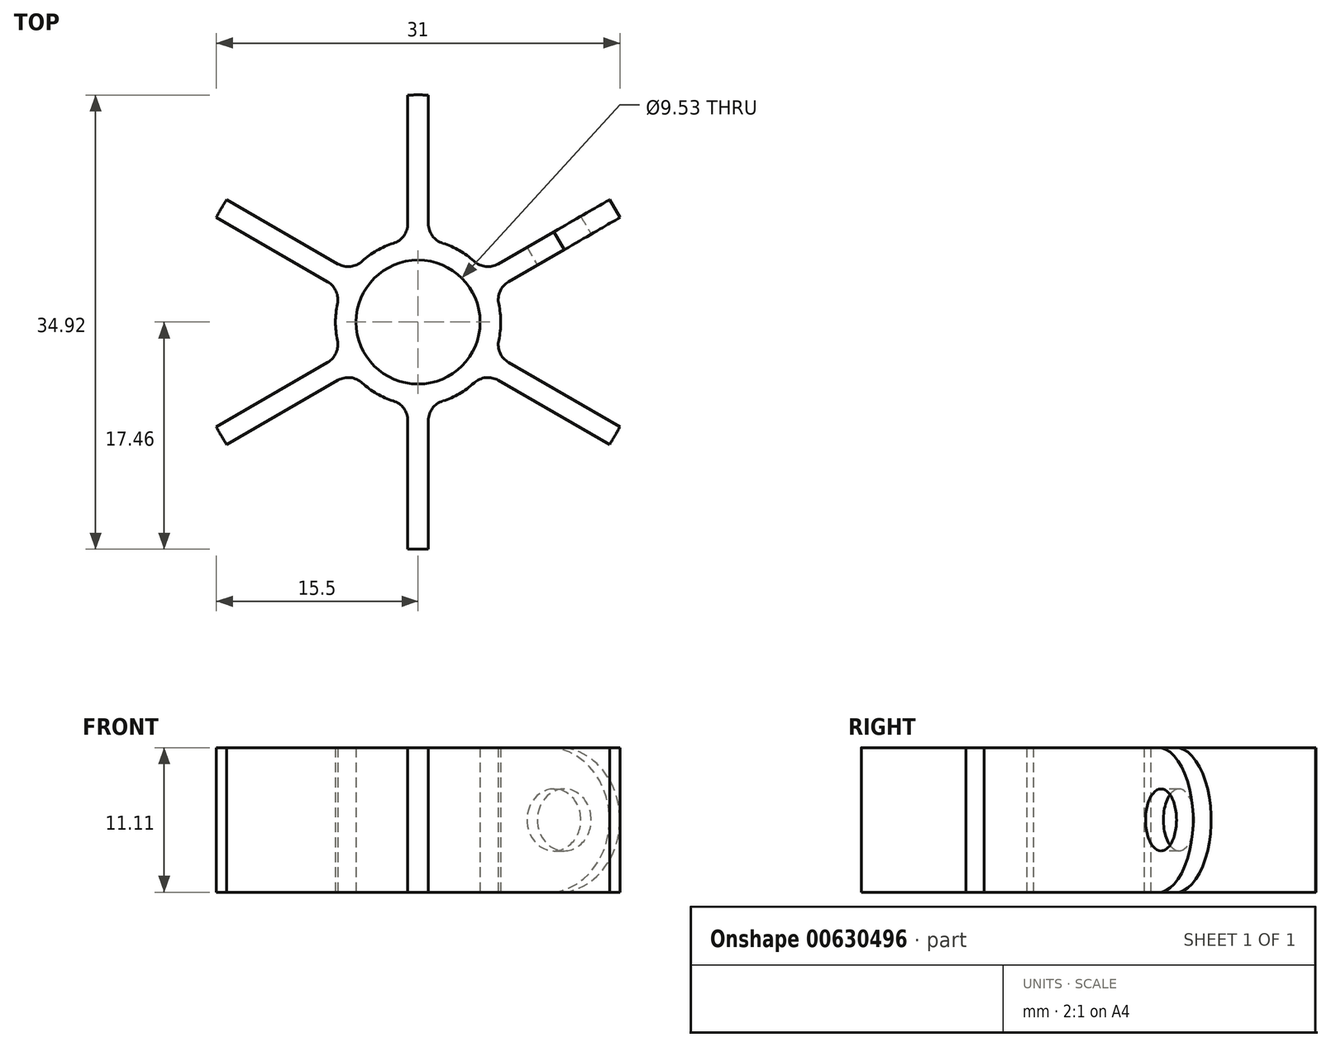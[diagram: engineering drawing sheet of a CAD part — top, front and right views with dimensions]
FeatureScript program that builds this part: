
annotation { "Feature Type Name" : "Feature", "Feature Type Description" : "" }
export const myFeature = defineFeature(function(context is Context, id is Id, definition is map)
    precondition{}
    {
        {
            var Q0;
            Q0=qCreatedBy(makeId("Top.planeOp"),FACE);
            var sketch = newSketch(context, id + "F0", { "sketchPlane" : qUnion([Q0])});
            skArc(sketch, "E0", {"start": v(-0.8, 6.3) * mm, "mid": v(-3.17, 5.5) * mm, "end": v(-5.06, 3.84) * mm});
            skLineSegment(sketch, "E1", {"start": v(0, 0) * mm, "end": v(0, 17.46) * mm, "construction": true});
            skArc(sketch, "E2", {"start": v(0.8, 17.44) * mm, "mid": v(0, 17.46) * mm, "end": v(-0.8, 17.44) * mm});
            skLineSegment(sketch, "E3", {"start": v(-0.8, 17.44) * mm, "end": v(-0.8, 6.3) * mm});
            skLineSegment(sketch, "E4", {"start": v(0.8, 17.44) * mm, "end": v(0.8, 6.3) * mm});
            skLineSegment(sketch, "E5.1.0", {"start": v(-14.71, 9.4) * mm, "end": v(-5.06, 3.84) * mm});
            skLineSegment(sketch, "E5.1.1", {"start": v(-15.5, 8.03) * mm, "end": v(-5.85, 2.46) * mm});
            skArc(sketch, "E5.1.2", {"start": v(-14.71, 9.4) * mm, "mid": v(-15.12, 8.73) * mm, "end": v(-15.5, 8.03) * mm});
            skLineSegment(sketch, "E5.1.3", {"start": v(0, 0) * mm, "end": v(-15.12, 8.73) * mm, "construction": true});
            skLineSegment(sketch, "E5.2.0", {"start": v(-15.5, -8.03) * mm, "end": v(-5.85, -2.46) * mm});
            skLineSegment(sketch, "E5.2.1", {"start": v(-14.71, -9.4) * mm, "end": v(-5.06, -3.84) * mm});
            skArc(sketch, "E5.2.2", {"start": v(-15.5, -8.03) * mm, "mid": v(-15.12, -8.73) * mm, "end": v(-14.71, -9.4) * mm});
            skLineSegment(sketch, "E5.2.3", {"start": v(0, 0) * mm, "end": v(-15.12, -8.73) * mm, "construction": true});
            skLineSegment(sketch, "E5.3.0", {"start": v(-0.8, -17.44) * mm, "end": v(-0.8, -6.3) * mm});
            skLineSegment(sketch, "E5.3.1", {"start": v(0.8, -17.44) * mm, "end": v(0.8, -6.3) * mm});
            skArc(sketch, "E5.3.2", {"start": v(-0.8, -17.44) * mm, "mid": v(0, -17.46) * mm, "end": v(0.8, -17.44) * mm});
            skLineSegment(sketch, "E5.3.3", {"start": v(0, 0) * mm, "end": v(0, -17.46) * mm, "construction": true});
            skLineSegment(sketch, "E5.4.0", {"start": v(14.71, -9.4) * mm, "end": v(5.06, -3.84) * mm});
            skLineSegment(sketch, "E5.4.1", {"start": v(15.5, -8.03) * mm, "end": v(5.85, -2.46) * mm});
            skArc(sketch, "E5.4.2", {"start": v(14.71, -9.4) * mm, "mid": v(15.12, -8.73) * mm, "end": v(15.5, -8.03) * mm});
            skLineSegment(sketch, "E5.4.3", {"start": v(0, 0) * mm, "end": v(15.12, -8.73) * mm, "construction": true});
            skLineSegment(sketch, "E5.5.0", {"start": v(15.5, 8.03) * mm, "end": v(5.85, 2.46) * mm});
            skLineSegment(sketch, "E5.5.1", {"start": v(14.71, 9.4) * mm, "end": v(5.06, 3.84) * mm});
            skArc(sketch, "E5.5.2", {"start": v(15.5, 8.03) * mm, "mid": v(15.12, 8.73) * mm, "end": v(14.71, 9.4) * mm});
            skLineSegment(sketch, "E5.5.3", {"start": v(0, 0) * mm, "end": v(15.12, 8.73) * mm, "construction": true});
            skArc(sketch, "E6.trimOffspring", {"start": v(5.06, 3.84) * mm, "mid": v(3.17, 5.5) * mm, "end": v(0.8, 6.3) * mm});
            skArc(sketch, "E7.trimOffspring", {"start": v(5.85, -2.46) * mm, "mid": v(6.35, 0) * mm, "end": v(5.85, 2.46) * mm});
            skArc(sketch, "E8.trimOffspring", {"start": v(0.8, -6.3) * mm, "mid": v(3.17, -5.5) * mm, "end": v(5.06, -3.84) * mm});
            skArc(sketch, "E9.trimOffspring", {"start": v(-5.06, -3.84) * mm, "mid": v(-3.18, -5.5) * mm, "end": v(-0.8, -6.3) * mm});
            skArc(sketch, "E10.trimOffspring", {"start": v(-5.85, 2.46) * mm, "mid": v(-6.35, 0) * mm, "end": v(-5.85, -2.46) * mm});
            skCircle(sketch, "E11", {"center": v(0, 0) * mm, "radius": 4.76 * mm});
            skSolve(sketch);
        }
        {
            var Q0;
            Q0=makeQuery(id+"F0.imprint","IMPRINT",FACE,{"disambiguationData":[TD([[makeQuery(id+"F0.imprint","IMPRINT",EDGE,{"derivedFrom":sQuery(id+"F0.wireOp",EDGE,"E0")}),1.0]])]});
            extrude(context, id + "F1", {"entities" : qUnion([Q0]), "depth" : 11.1 * mm, "offsetDistance" : 25.4 * mm});
        }
        {
            var Q0;
            Q0=makeQuery(id+"F1.opExtrude","SWEPT_EDGE",EDGE,{"disambiguationData":[OSD([sQuery(id+"F0.wireOp",EDGE,"E0"),sQuery(id+"F0.wireOp",EDGE,"E5.1.0")])]});
            var Q1;
            Q1=makeQuery(id+"F1.opExtrude","SWEPT_EDGE",EDGE,{"disambiguationData":[OSD([sQuery(id+"F0.wireOp",EDGE,"E4"),sQuery(id+"F0.wireOp",EDGE,"E6.trimOffspring")])]});
            var Q2;
            Q2=makeQuery(id+"F1.opExtrude","SWEPT_EDGE",EDGE,{"disambiguationData":[OSD([sQuery(id+"F0.wireOp",EDGE,"E5.5.1"),sQuery(id+"F0.wireOp",EDGE,"E6.trimOffspring")])]});
            var Q3;
            Q3=makeQuery(id+"F1.opExtrude","SWEPT_EDGE",EDGE,{"disambiguationData":[OSD([sQuery(id+"F0.wireOp",EDGE,"E5.4.1"),sQuery(id+"F0.wireOp",EDGE,"E7.trimOffspring")])]});
            var Q4;
            Q4=makeQuery(id+"F1.opExtrude","SWEPT_EDGE",EDGE,{"disambiguationData":[OSD([sQuery(id+"F0.wireOp",EDGE,"E5.5.0"),sQuery(id+"F0.wireOp",EDGE,"E7.trimOffspring")])]});
            var Q5;
            Q5=makeQuery(id+"F1.opExtrude","SWEPT_EDGE",EDGE,{"disambiguationData":[OSD([sQuery(id+"F0.wireOp",EDGE,"E5.3.1"),sQuery(id+"F0.wireOp",EDGE,"E8.trimOffspring")])]});
            var Q6;
            Q6=makeQuery(id+"F1.opExtrude","SWEPT_EDGE",EDGE,{"disambiguationData":[OSD([sQuery(id+"F0.wireOp",EDGE,"E5.4.0"),sQuery(id+"F0.wireOp",EDGE,"E8.trimOffspring")])]});
            var Q7;
            Q7=makeQuery(id+"F1.opExtrude","SWEPT_EDGE",EDGE,{"disambiguationData":[OSD([sQuery(id+"F0.wireOp",EDGE,"E5.3.0"),sQuery(id+"F0.wireOp",EDGE,"E9.trimOffspring")])]});
            var Q8;
            Q8=makeQuery(id+"F1.opExtrude","SWEPT_EDGE",EDGE,{"disambiguationData":[OSD([sQuery(id+"F0.wireOp",EDGE,"E5.2.1"),sQuery(id+"F0.wireOp",EDGE,"E9.trimOffspring")])]});
            var Q9;
            Q9=makeQuery(id+"F1.opExtrude","SWEPT_EDGE",EDGE,{"disambiguationData":[OSD([sQuery(id+"F0.wireOp",EDGE,"E5.2.0"),sQuery(id+"F0.wireOp",EDGE,"E10.trimOffspring")])]});
            var Q10;
            Q10=makeQuery(id+"F1.opExtrude","SWEPT_EDGE",EDGE,{"disambiguationData":[OSD([sQuery(id+"F0.wireOp",EDGE,"E5.1.1"),sQuery(id+"F0.wireOp",EDGE,"E10.trimOffspring")])]});
            var Q11;
            Q11=makeQuery(id+"F1.opExtrude","SWEPT_EDGE",EDGE,{"disambiguationData":[OSD([sQuery(id+"F0.wireOp",EDGE,"E0"),sQuery(id+"F0.wireOp",EDGE,"E3")])]});
            fillet(context, id + "F2", {"entities" : qUnion([Q0, Q1, Q2, Q3, Q4, Q5, Q6, Q7, Q8, Q9, Q10, Q11]), "radius" : 1.59 * mm, "tangentPropagation" : true, "allowEdgeOverflow" : false});
        }
        {
            var Q0;
            Q0=makeQuery(id+"F1.opExtrude","SWEPT_FACE",FACE,{"disambiguationData":[OSD([sQuery(id+"F0.wireOp",EDGE,"E5.5.0")])]});
            var sketch = newSketch(context, id + "F3", { "sketchPlane" : qUnion([Q0])});
            skCircle(sketch, "E12", {"center": v(12.5, 5.56) * mm, "radius": 2.38 * mm});
            skPoint(sketch, "E12.centerSnap0", {"position": v(17.44, 5.56) * mm});
            skPoint(sketch, "E12.centerSnap1", {"position": v(12.5, 11.11) * mm});
            skArc(sketch, "E13", {"start": v(12.5, 0) * mm, "mid": v(17.44, 5.56) * mm, "end": v(12.5, 11.11) * mm});
            skLineSegment(sketch, "E14", {"start": v(12.5, 11.11) * mm, "end": v(12.5, 12.57) * mm});
            skLineSegment(sketch, "E15", {"start": v(12.5, 12.57) * mm, "end": v(18.77, 12.57) * mm});
            skLineSegment(sketch, "E16", {"start": v(18.77, 12.57) * mm, "end": v(18.77, -1.82) * mm});
            skLineSegment(sketch, "E17", {"start": v(18.77, -1.82) * mm, "end": v(12.5, -1.82) * mm});
            skLineSegment(sketch, "E18", {"start": v(12.5, -1.82) * mm, "end": v(12.5, 0) * mm});
            skSolve(sketch);
        }
        {
            var Q0;
            Q0 = qSketchRegion(id + "F3", true);
            extrude(context, id + "F4", {"entities" : qUnion([Q0]), "operationType" : NewBodyOperationType.REMOVE, "endBound" : BoundingType.THROUGH_ALL, "oppositeDirection" : true, "depth" : 25.4 * mm, "offsetDistance" : 25.4 * mm});
        }
    });
